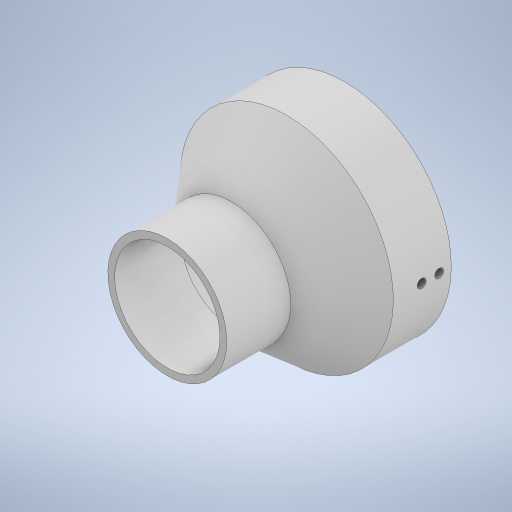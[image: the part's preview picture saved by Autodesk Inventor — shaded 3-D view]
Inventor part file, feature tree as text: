
AUTODESK INVENTOR PART (.ipt)
format: ipt  version: 2023 (Build 270158030, 158C)  size: 275,456 bytes
history: native  units: in
note: dims shown in document units (in); Inventor stores cm internally (conversion verified against a paired STEP export)
features: sketch x2, revolve x1, extrude x1
ambient origin geometry x8: Origin, YZ Plane, XZ Plane, XY Plane, X Axis, Y Axis, Z Axis, Center Point
bodies: Solid1 (feature_tree)
feature tree (4):
  revolve  "Revolution1"  [1 undecoded]
  extrude  "Extrusion1"  Depth=0.3937in
  sketch  "Sketch1"  dims[d0=2.375in d1=4.5in]
  sketch  "Sketch3"  dims[d2=1.5in d3=1.25in d4=0.154in d5=4.0in d6=2.0in d7=90.0deg d8=0.1969in d9=0.1969in d10=0.2756in d11=0.3937in d12=0.0in d13=0.0in]
note: 1 required parameter value undecoded (feature->parameter linkage not recoverable at this tier; creation-order binding heuristic only, values carry confidence <= 0.55)
